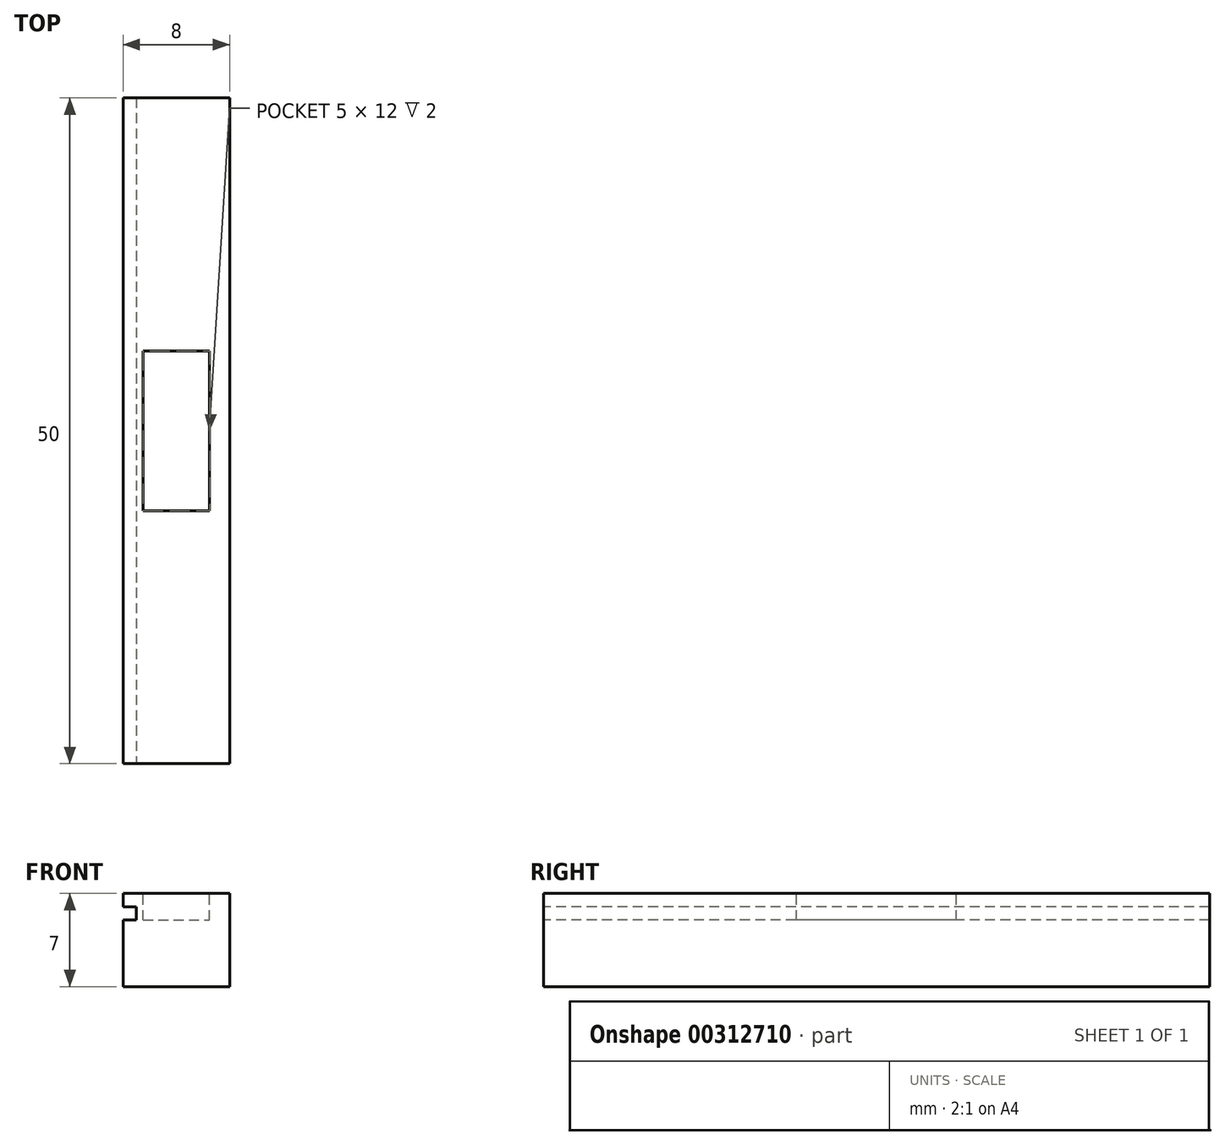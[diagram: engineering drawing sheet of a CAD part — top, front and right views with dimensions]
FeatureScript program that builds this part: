
annotation { "Feature Type Name" : "Feature", "Feature Type Description" : "" }
export const myFeature = defineFeature(function(context is Context, id is Id, definition is map)
    precondition{}
    {
        {
            var Q0;
            Q0=qCreatedBy(makeId("Top.planeOp"),FACE);
            var sketch = newSketch(context, id + "F0", { "sketchPlane" : qUnion([Q0])});
            skLineSegment(sketch, "E0.bottom", {"start": v(4, -25) * mm, "end": v(-4, -25) * mm});
            skLineSegment(sketch, "E0.top", {"start": v(4, 25) * mm, "end": v(-4, 25) * mm});
            skLineSegment(sketch, "E0.left", {"start": v(4, -25) * mm, "end": v(4, 25) * mm});
            skLineSegment(sketch, "E0.right", {"start": v(-4, -25) * mm, "end": v(-4, 25) * mm});
            skPoint(sketch, "E0.middle", {"position": v(0, 0) * mm});
            skSolve(sketch);
        }
        {
            var Q0;
            Q0=makeQuery(id+"F0.imprint","IMPRINT",FACE,{"disambiguationData":[TD([[makeQuery(id+"F0.imprint","IMPRINT",EDGE,{"derivedFrom":sQuery(id+"F0.wireOp",EDGE,"E0.bottom")}),-1.0]])]});
            extrude(context, id + "F1", {"entities" : qUnion([Q0]), "depth" : 7 * mm});
        }
        {
            var Q0;
            Q0=makeQuery(id+"F1.opExtrude","SWEPT_FACE",FACE,{"disambiguationData":[OSD([sQuery(id+"F0.wireOp",EDGE,"E0.right")])]});
            var sketch = newSketch(context, id + "F2", { "sketchPlane" : qUnion([Q0])});
            skLineSegment(sketch, "E1.bottom", {"start": v(-25, 6) * mm, "end": v(25, 6) * mm});
            skLineSegment(sketch, "E1.top", {"start": v(-25, 5) * mm, "end": v(25, 5) * mm});
            skLineSegment(sketch, "E1.left", {"start": v(-25, 6) * mm, "end": v(-25, 5) * mm});
            skLineSegment(sketch, "E1.right", {"start": v(25, 6) * mm, "end": v(25, 5) * mm});
            skSolve(sketch);
        }
        {
            var Q0;
            Q0=makeQuery(id+"F2.imprint","IMPRINT",FACE,{"disambiguationData":[TD([[makeQuery(id+"F2.imprint","IMPRINT",EDGE,{"derivedFrom":sQuery(id+"F2.wireOp",EDGE,"E1.bottom")}),-1.0]])]});
            extrude(context, id + "F3", {"entities" : qUnion([Q0]), "operationType" : NewBodyOperationType.REMOVE, "oppositeDirection" : true, "depth" : 1 * mm});
        }
        {
            var Q0;
            Q0=makeQuery(id+"F1.opExtrude","CAP_FACE",FACE,{"disambiguationData":[OSD([sQuery(id+"F0.wireOp",EDGE,"E0.bottom"),sQuery(id+"F0.wireOp",EDGE,"E0.top"),sQuery(id+"F0.wireOp",EDGE,"E0.left"),sQuery(id+"F0.wireOp",EDGE,"E0.right")])],"isStart":false});
            var sketch = newSketch(context, id + "F4", { "sketchPlane" : qUnion([Q0])});
            skLineSegment(sketch, "E2.bottom", {"start": v(-2.5, 6) * mm, "end": v(2.5, 6) * mm});
            skLineSegment(sketch, "E2.top", {"start": v(-2.5, -6) * mm, "end": v(2.5, -6) * mm});
            skLineSegment(sketch, "E2.left", {"start": v(-2.5, 6) * mm, "end": v(-2.5, -6) * mm});
            skLineSegment(sketch, "E2.right", {"start": v(2.5, 6) * mm, "end": v(2.5, -6) * mm});
            skPoint(sketch, "E2.middle", {"position": v(0, 0) * mm});
            skSolve(sketch);
        }
        {
            var Q0;
            Q0=makeQuery(id+"F4.imprint","IMPRINT",FACE,{"disambiguationData":[TD([[makeQuery(id+"F4.imprint","IMPRINT",EDGE,{"derivedFrom":sQuery(id+"F4.wireOp",EDGE,"E2.bottom")}),-1.0]])]});
            extrude(context, id + "F5", {"entities" : qUnion([Q0]), "operationType" : NewBodyOperationType.REMOVE, "oppositeDirection" : true, "depth" : 2 * mm});
        }
    });
